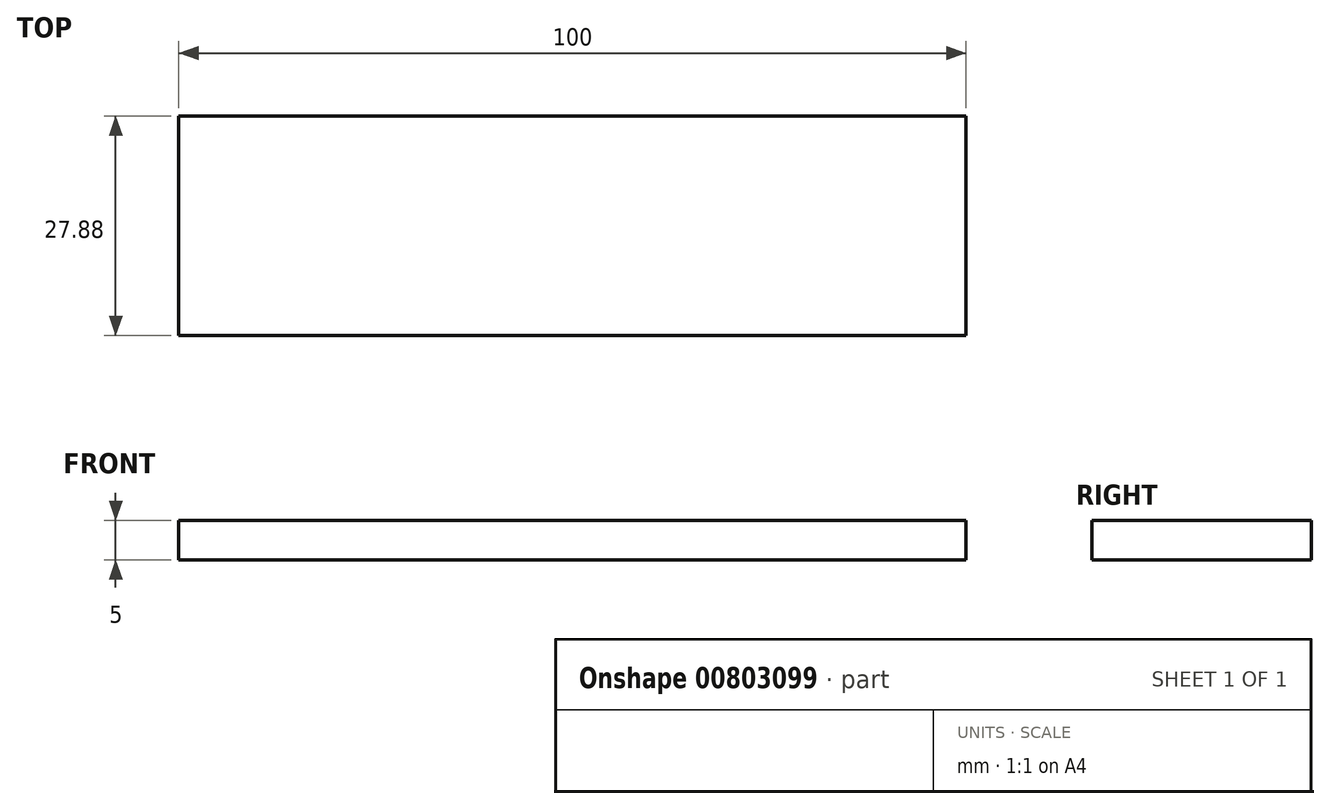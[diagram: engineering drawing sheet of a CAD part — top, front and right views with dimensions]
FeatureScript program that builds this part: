
annotation { "Feature Type Name" : "Feature", "Feature Type Description" : "" }
export const myFeature = defineFeature(function(context is Context, id is Id, definition is map)
    precondition{}
    {
        {
            var Q0;
            Q0=qCreatedBy(makeId("Top.planeOp"),FACE);
            var sketch = newSketch(context, id + "F0", { "sketchPlane" : qUnion([Q0])});
            skLineSegment(sketch, "E0.bottom", {"start": v(-50, 13.94) * mm, "end": v(50, 13.94) * mm});
            skLineSegment(sketch, "E0.top", {"start": v(-50, -13.94) * mm, "end": v(50, -13.94) * mm});
            skLineSegment(sketch, "E0.left", {"start": v(-50, 13.94) * mm, "end": v(-50, -13.94) * mm});
            skLineSegment(sketch, "E0.right", {"start": v(50, 13.94) * mm, "end": v(50, -13.94) * mm});
            skPoint(sketch, "E0.middle", {"position": v(0, 0) * mm});
            skSolve(sketch);
        }
        {
            var Q0;
            Q0=makeQuery(id+"F0.imprint","IMPRINT",FACE,{"disambiguationData":[TD([[makeQuery(id+"F0.imprint","IMPRINT",EDGE,{"derivedFrom":sQuery(id+"F0.wireOp",EDGE,"E0.bottom")}),-1.0]])]});
            extrude(context, id + "F1", {"entities" : qUnion([Q0]), "depth" : 5 * mm, "offsetDistance" : 25 * mm});
        }
    });
